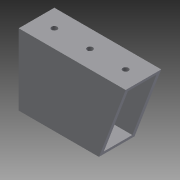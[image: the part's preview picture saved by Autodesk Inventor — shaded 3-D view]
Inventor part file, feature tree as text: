
AUTODESK INVENTOR PART (.ipt)
format: ipt  version: 2015 SP1 (Build 190203100, 203)  size: 97,792 bytes
history: native  units: in
note: dims shown in document units (in); Inventor stores cm internally (conversion verified against a paired STEP export)
features: sketch x2, extrude x1, hole x1, projected_geometry x1
ambient origin geometry x8: Origin, YZ Plane, XZ Plane, XY Plane, X Axis, Y Axis, Z Axis, Center Point
bodies: Solid1 (feature_tree)
feature tree (5):
  extrude  "Extrusion1"  Depth=1.0in
  hole  "Hole1"  [1 undecoded]
  sketch  "Sketch1"  dims[d0=2.0in d1=1.0in]
  sketch  "Sketch2"  dims[d2=1.8in d3=0.8in d4=0.1in d5=0.1in d6=3.0in d7=0.0in d8=0.5in d9=0.5in d10=0.5in d11=0.5in d12=1.5in d13=2.5in d14=0.1562in d15=0.75in d16=0.375in d17=0.25in d18=0.5635in d19=1.0in d20=0.8108in]
  projected_geometry  "Projected Loop1"
note: 1 required parameter value undecoded (feature->parameter linkage not recoverable at this tier; creation-order binding heuristic only, values carry confidence <= 0.55)
